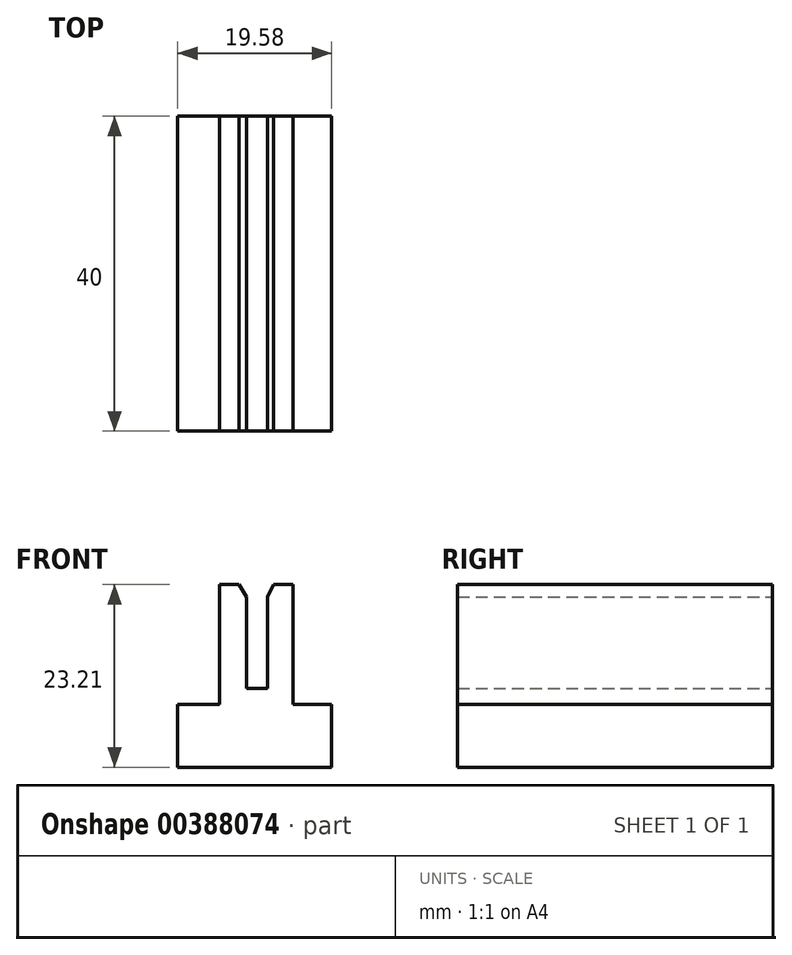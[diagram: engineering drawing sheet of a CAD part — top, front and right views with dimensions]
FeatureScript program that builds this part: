
annotation { "Feature Type Name" : "Feature", "Feature Type Description" : "" }
export const myFeature = defineFeature(function(context is Context, id is Id, definition is map)
    precondition{}
    {
        {
            var Q0;
            Q0=qCreatedBy(makeId("Front.planeOp"),FACE);
            var sketch = newSketch(context, id + "F0", { "sketchPlane" : qUnion([Q0])});
            skPoint(sketch, "E0", {"position": v(-10.6, 0) * mm});
            skPoint(sketch, "E1", {"position": v(9, 0) * mm});
            skLineSegment(sketch, "E2", {"start": v(-10.6, 0) * mm, "end": v(9, 0) * mm});
            skPoint(sketch, "E3", {"position": v(9, 7.97) * mm});
            skPoint(sketch, "E4", {"position": v(-10.6, 7.97) * mm});
            skLineSegment(sketch, "E5", {"start": v(-10.6, 0) * mm, "end": v(-10.6, 7.97) * mm});
            skLineSegment(sketch, "E6", {"start": v(9, 7.97) * mm, "end": v(9, 0) * mm});
            skPoint(sketch, "E7", {"position": v(-5.27, 7.97) * mm});
            skPoint(sketch, "E8", {"position": v(4.08, 7.97) * mm});
            skLineSegment(sketch, "E9", {"start": v(-10.6, 7.97) * mm, "end": v(-5.27, 7.97) * mm});
            skLineSegment(sketch, "E10", {"start": v(4.08, 7.97) * mm, "end": v(9, 7.97) * mm});
            skPoint(sketch, "E11", {"position": v(-5.27, 23.2) * mm});
            skPoint(sketch, "E12", {"position": v(4.08, 23.2) * mm});
            skPoint(sketch, "E13", {"position": v(-23.23, 27.3) * mm});
            skLineSegment(sketch, "E14", {"start": v(4.08, 7.97) * mm, "end": v(4.08, 23.2) * mm});
            skLineSegment(sketch, "E15", {"start": v(-5.27, 7.97) * mm, "end": v(-5.27, 23.2) * mm});
            skPoint(sketch, "E16", {"position": v(-2.8, 23.2) * mm});
            skPoint(sketch, "E17", {"position": v(1.6, 23.2) * mm});
            skLineSegment(sketch, "E18", {"start": v(-5.27, 23.2) * mm, "end": v(-2.8, 23.2) * mm});
            skLineSegment(sketch, "E19", {"start": v(1.6, 23.2) * mm, "end": v(4.08, 23.2) * mm});
            skPoint(sketch, "E20", {"position": v(-1.8, 21.64) * mm});
            skPoint(sketch, "E21", {"position": v(0.84, 21.64) * mm});
            skPoint(sketch, "E22", {"position": v(-1.8, 10.04) * mm});
            skPoint(sketch, "E23", {"position": v(0.84, 10.04) * mm});
            skLineSegment(sketch, "E24", {"start": v(-2.8, 23.2) * mm, "end": v(-1.8, 21.64) * mm});
            skLineSegment(sketch, "E25", {"start": v(-1.8, 21.64) * mm, "end": v(-1.8, 10.04) * mm});
            skLineSegment(sketch, "E26", {"start": v(1.6, 23.2) * mm, "end": v(0.84, 21.64) * mm});
            skLineSegment(sketch, "E27", {"start": v(0.84, 21.64) * mm, "end": v(0.84, 10.04) * mm});
            skLineSegment(sketch, "E28", {"start": v(0.84, 10.04) * mm, "end": v(-1.8, 10.04) * mm});
            skSolve(sketch);
        }
        {
            var Q0;
            Q0 = qSketchRegion(id + "F0", true);
            extrude(context, id + "F1", {"entities" : qUnion([Q0]), "depth" : 40 * mm});
        }
        {
            var Q0;
            Q0=qCreatedBy(makeId("Right.planeOp"),FACE);
            var sketch = newSketch(context, id + "F2", { "sketchPlane" : qUnion([Q0])});
            skCircle(sketch, "E29", {"center": v(-35.32, 18.27) * mm, "radius": 2.5 * mm});
            skSolve(sketch);
        }
        {
            var Q0;
            Q0=sQuery(id+"F2.wireOp",EDGE,"E29");
            extrude(context, id + "F3", {"bodyType" : ToolBodyType.SURFACE, "surfaceEntities" : qUnion([Q0]), "endBound" : BoundingType.SYMMETRIC, "depth" : 21.84 * mm});
        }
        {
            var Q0;
            Q0=qCreatedBy(makeId("Top.planeOp"),FACE);
            var sketch = newSketch(context, id + "F4", { "sketchPlane" : qUnion([Q0])});
            skPoint(sketch, "E30", {"position": v(-1.85, -25.4) * mm});
            skPoint(sketch, "E31", {"position": v(1.7, -25.47) * mm});
            skPoint(sketch, "E32", {"position": v(-2.95, -25.47) * mm});
            skPoint(sketch, "E33", {"position": v(-2.95, -32.49) * mm});
            skPoint(sketch, "E34", {"position": v(1.8, -32.49) * mm});
            skArc(sketch, "E35", {"start": v(1.8, -32.49) * mm, "mid": v(-0.58, -25.1) * mm, "end": v(-2.95, -32.49) * mm});
            skSolve(sketch);
        }
        {
            var Q0;
            Q0=sQuery(id+"F4.wireOp",EDGE,"E35");
            extrude(context, id + "F5", {"bodyType" : ToolBodyType.SURFACE, "surfaceEntities" : qUnion([Q0]), "depth" : 21.84 * mm});
        }
    });
